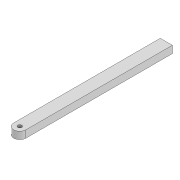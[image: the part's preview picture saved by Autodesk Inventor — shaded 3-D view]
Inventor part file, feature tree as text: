
AUTODESK INVENTOR PART (.ipt)
format: ipt  version: 2022 (Build 260153000, 153)  size: 96,256 bytes
history: native  units: mm
features: extrude x2, sketch x2
ambient origin geometry x8: Origin, YZ Plane, XZ Plane, XY Plane, X Axis, Y Axis, Z Axis, Center Point
bodies: Solid1 (feature_tree)
feature tree (4):
  extrude  "Extrusion1"  Depth=3.3mm
  extrude  "Extrusion2"  Depth=6.0mm
  sketch  "Sketch1"  dims[d0=3.3mm d1=3.3mm]
  sketch  "Sketch3"  dims[d2=10.0mm d3=261.6mm d4=3.3mm d5=153.559mm d6=6.0mm d7=0.0mm d8=100.0mm d9=0.0mm]
